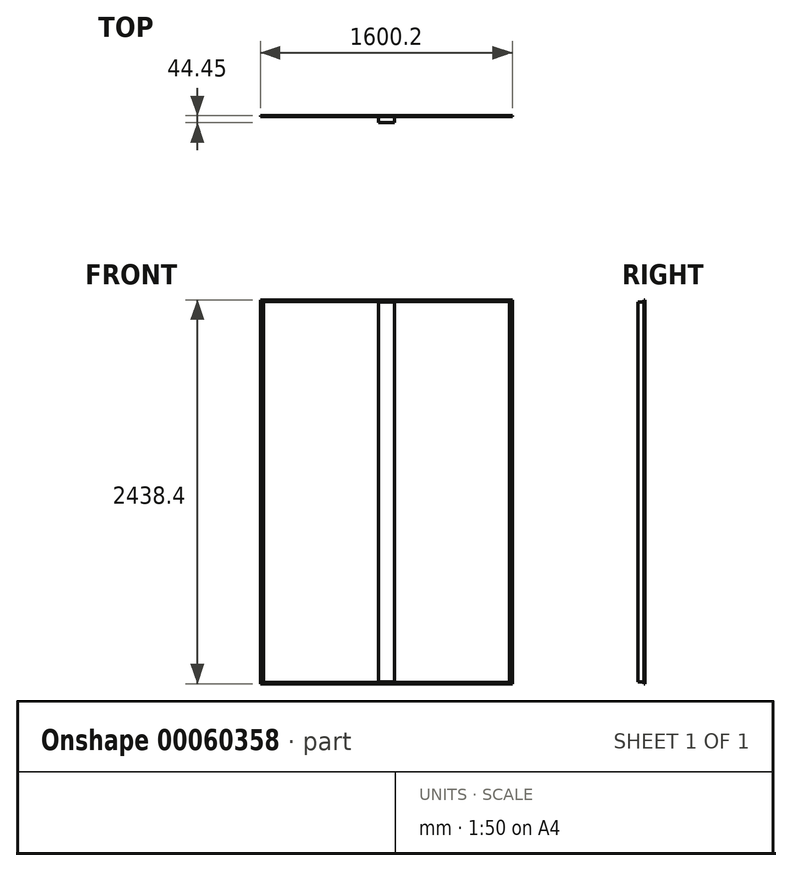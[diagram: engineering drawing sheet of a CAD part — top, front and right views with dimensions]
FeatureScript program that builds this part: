
annotation { "Feature Type Name" : "Feature", "Feature Type Description" : "" }
export const myFeature = defineFeature(function(context is Context, id is Id, definition is map)
    precondition{}
    {
        {
            var Q0;
            Q0=qCreatedBy(makeId("Front.planeOp"),FACE);
            var sketch = newSketch(context, id + "F0", { "sketchPlane" : qUnion([Q0])});
            skLineSegment(sketch, "E0.rect.bottom", {"start": v(800.1, -1219.2) * mm, "end": v(-800.1, -1219.2) * mm});
            skLineSegment(sketch, "E0.rect.top", {"start": v(800.1, 1219.2) * mm, "end": v(-800.1, 1219.2) * mm});
            skLineSegment(sketch, "E0.rect.left", {"start": v(800.1, -1219.2) * mm, "end": v(800.1, 1219.2) * mm});
            skLineSegment(sketch, "E0.rect.right", {"start": v(-800.1, -1219.2) * mm, "end": v(-800.1, 1219.2) * mm});
            skPoint(sketch, "E0.rect.middle", {"position": v(0, 0) * mm});
            skSolve(sketch);
        }
        {
            var Q0;
            Q0=makeQuery(id+"F0.imprint","IMPRINT",FACE,{"disambiguationData":[TD([[makeQuery(id+"F0.imprint","IMPRINT",EDGE,{"derivedFrom":sQuery(id+"F0.wireOp",EDGE,"E0.rect.bottom")}),-1.0]])]});
            extrude(context, id + "F1", {"entities" : qUnion([Q0]), "depth" : 6.35 * mm});
        }
        {
            var Q0;
            Q0=qCreatedBy(makeId("Front.planeOp"),FACE);
            var sketch = newSketch(context, id + "F2", { "sketchPlane" : qUnion([Q0])});
            skLineSegment(sketch, "E1.rect.bottom", {"start": v(50.8, -1206.5) * mm, "end": v(-50.8, -1206.5) * mm});
            skLineSegment(sketch, "E1.rect.top", {"start": v(50.8, 1206.5) * mm, "end": v(-50.8, 1206.5) * mm});
            skLineSegment(sketch, "E1.rect.left", {"start": v(50.8, -1206.5) * mm, "end": v(50.8, 1206.5) * mm});
            skLineSegment(sketch, "E1.rect.right", {"start": v(-50.8, -1206.5) * mm, "end": v(-50.8, 1206.5) * mm});
            skPoint(sketch, "E1.rect.middle", {"position": v(0, 0) * mm});
            skSolve(sketch);
        }
        {
            var Q0;
            Q0=makeQuery(id+"F2.imprint","IMPRINT",FACE,{"disambiguationData":[TD([[makeQuery(id+"F2.imprint","IMPRINT",EDGE,{"derivedFrom":sQuery(id+"F2.wireOp",EDGE,"E1.rect.bottom")}),-1.0]])]});
            extrude(context, id + "F3", {"entities" : qUnion([Q0]), "depth" : 44.45 * mm});
        }
        {
            var Q0;
            Q0=qCreatedBy(makeId("Front.planeOp"),FACE);
            var sketch = newSketch(context, id + "F4", { "sketchPlane" : qUnion([Q0])});
            skLineSegment(sketch, "E2.rect.bottom", {"start": v(781.05, -1209.67) * mm, "end": v(-781.05, -1209.67) * mm});
            skLineSegment(sketch, "E2.rect.top", {"start": v(781.05, 1209.67) * mm, "end": v(-781.05, 1209.67) * mm});
            skLineSegment(sketch, "E2.rect.left", {"start": v(781.05, -1209.67) * mm, "end": v(781.05, 1209.67) * mm});
            skLineSegment(sketch, "E2.rect.right", {"start": v(-781.05, -1209.67) * mm, "end": v(-781.05, 1209.67) * mm});
            skPoint(sketch, "E2.rect.middle", {"position": v(0, 0) * mm});
            skSolve(sketch);
        }
        {
            var Q0;
            Q0=makeQuery(id+"F4.imprint","IMPRINT",FACE,{"disambiguationData":[TD([[makeQuery(id+"F4.imprint","IMPRINT",EDGE,{"derivedFrom":sQuery(id+"F4.wireOp",EDGE,"E2.rect.bottom")}),-1.0]])]});
            extrude(context, id + "F5", {"entities" : qUnion([Q0]), "depth" : 6.35 * mm});
        }
    });
